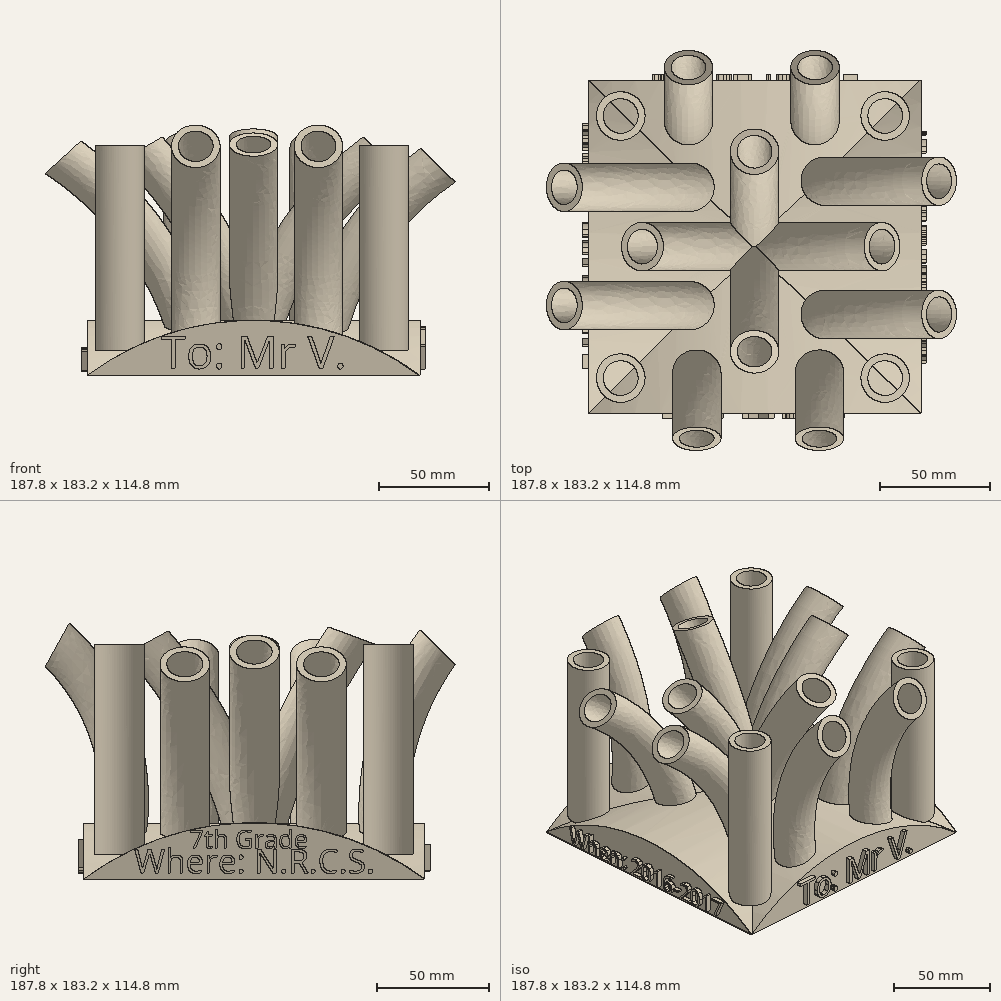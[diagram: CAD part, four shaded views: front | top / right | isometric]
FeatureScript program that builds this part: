
annotation { "Feature Type Name" : "Feature", "Feature Type Description" : "" }
export const myFeature = defineFeature(function(context is Context, id is Id, definition is map)
    precondition{}
    {
        {
            var Q0;
            Q0=qCreatedBy(makeId("Front.planeOp"),FACE);
            var sketch = newSketch(context, id + "F0", { "sketchPlane" : qUnion([Q0])});
            skLineSegment(sketch, "E0", {"start": v(0, -11.51) * mm, "end": v(-76.2, -11.51) * mm});
            skLineSegment(sketch, "E1", {"start": v(0, -11.51) * mm, "end": v(76.2, -11.51) * mm});
            skArc(sketch, "E2", {"start": v(76.2, -11.51) * mm, "mid": v(0, 13.89) * mm, "end": v(-76.2, -11.51) * mm});
            skSolve(sketch);
        }
        {
            var Q0;
            Q0 = qSketchRegion(id + "F0", true);
            extrude(context, id + "F1", {"entities" : qUnion([Q0]), "depth" : 76.2 * mm, "hasSecondDirection" : true, "secondDirectionOppositeDirection" : true, "secondDirectionDepth" : 76.2 * mm});
        }
        {
            var Q0;
            Q0=qCreatedBy(makeId("Right.planeOp"),FACE);
            var sketch = newSketch(context, id + "F2", { "sketchPlane" : qUnion([Q0])});
            skLineSegment(sketch, "E3", {"start": v(0, -11.22) * mm, "end": v(76.2, -11.22) * mm});
            skLineSegment(sketch, "E4", {"start": v(0, -11.22) * mm, "end": v(-76.2, -11.22) * mm});
            skArc(sketch, "E5", {"start": v(76.2, -11.22) * mm, "mid": v(0, 14.06) * mm, "end": v(-76.2, -11.22) * mm});
            skSolve(sketch);
        }
        {
            var Q0;
            Q0 = qSketchRegion(id + "F2", true);
            extrude(context, id + "F3", {"entities" : qUnion([Q0]), "operationType" : NewBodyOperationType.ADD, "depth" : 76.2 * mm, "hasSecondDirection" : true, "secondDirectionOppositeDirection" : true, "secondDirectionDepth" : 76.2 * mm});
        }
        {
            var Q0;
            Q0=qCreatedBy(makeId("Top.planeOp"),FACE);
            var sketch = newSketch(context, id + "F4", { "sketchPlane" : qUnion([Q0])});
            skCircle(sketch, "E6", {"center": v(0, 0) * mm, "radius": 11.11 * mm});
            skCircle(sketch, "E7", {"center": v(0, 0) * mm, "radius": 7.94 * mm});
            skSolve(sketch);
        }
        {
            var Q0;
            Q0=qCreatedBy(makeId("Front.planeOp"),FACE);
            var sketch = newSketch(context, id + "F5", { "sketchPlane" : qUnion([Q0])});
            skArc(sketch, "E8", {"start": v(0, 0) * mm, "mid": v(-19.55, 49.52) * mm, "end": v(-51.37, 92.2) * mm});
            skSolve(sketch);
        }
        {
            var Q0;
            Q0 = qSketchRegion(id + "F4", true);
            var Q1;
            Q1 = qConstructionFilter(qBodyType(qCreatedBy(id + "F5" ,EDGE), BodyType.WIRE), ConstructionObject.NO);
            sweep(context, id + "F6", {"operationType" : NewBodyOperationType.ADD, "profiles" : qUnion([Q0]), "path" : qUnion([Q1])});
        }
        {
            var Q0;
            Q0=qCreatedBy(makeId("Front.planeOp"),FACE);
            var sketch = newSketch(context, id + "F7", { "sketchPlane" : qUnion([Q0])});
            skArc(sketch, "E9", {"start": v(58.34, 90.31) * mm, "mid": v(20.67, 50.65) * mm, "end": v(0, 0) * mm});
            skSolve(sketch);
        }
        {
            var Q0;
            Q0 = qSketchRegion(id + "F4", true);
            var Q1;
            Q1 = qConstructionFilter(qBodyType(qCreatedBy(id + "F7" ,EDGE), BodyType.WIRE), ConstructionObject.NO);
            sweep(context, id + "F8", {"operationType" : NewBodyOperationType.ADD, "profiles" : qUnion([Q0]), "path" : qUnion([Q1])});
        }
        {
            var Q0;
            Q0=qCreatedBy(makeId("Right.planeOp"),FACE);
            var sketch = newSketch(context, id + "F9", { "sketchPlane" : qUnion([Q0])});
            skArc(sketch, "E10", {"start": v(1.27, 0) * mm, "mid": v(-16.91, 50.52) * mm, "end": v(-47, 94.99) * mm});
            skSolve(sketch);
        }
        {
            var Q0;
            Q0 = qSketchRegion(id + "F4", true);
            var Q1;
            Q1 = qConstructionFilter(qBodyType(qCreatedBy(id + "F9" ,EDGE), BodyType.WIRE), ConstructionObject.NO);
            sweep(context, id + "F10", {"operationType" : NewBodyOperationType.ADD, "profiles" : qUnion([Q0]), "path" : qUnion([Q1])});
        }
        {
            var Q0;
            Q0=qCreatedBy(makeId("Right.planeOp"),FACE);
            var sketch = newSketch(context, id + "F11", { "sketchPlane" : qUnion([Q0])});
            skArc(sketch, "E11", {"start": v(43.44, 97.68) * mm, "mid": v(17.36, 50.78) * mm, "end": v(0, 0) * mm});
            skSolve(sketch);
        }
        {
            var Q0;
            Q0 = qSketchRegion(id + "F4", true);
            var Q1;
            Q1 = qConstructionFilter(qBodyType(qCreatedBy(id + "F11" ,EDGE), BodyType.WIRE), ConstructionObject.NO);
            sweep(context, id + "F12", {"operationType" : NewBodyOperationType.ADD, "profiles" : qUnion([Q0]), "path" : qUnion([Q1])});
        }
        {
            var Q0;
            Q0=qCreatedBy(makeId("Top.planeOp"),FACE);
            var sketch = newSketch(context, id + "F13", { "sketchPlane" : qUnion([Q0])});
            skCircle(sketch, "E12", {"center": v(-26.33, 27.16) * mm, "radius": 11.11 * mm});
            skCircle(sketch, "E13", {"center": v(-26.33, 27.16) * mm, "radius": 7.94 * mm});
            skCircle(sketch, "E14", {"center": v(-26.33, -26.98) * mm, "radius": 11.11 * mm});
            skCircle(sketch, "E15", {"center": v(-26.33, -26.98) * mm, "radius": 7.94 * mm});
            skSolve(sketch);
        }
        {
            var Q0;
            Q0=qCreatedBy(makeId("Front.planeOp"),FACE);
            var sketch = newSketch(context, id + "F14", { "sketchPlane" : qUnion([Q0])});
            skArc(sketch, "E16", {"start": v(-26.38, 0) * mm, "mid": v(-48.5, 49.92) * mm, "end": v(-87.15, 88.47) * mm});
            skSolve(sketch);
        }
        {
            var Q0;
            Q0 = qSketchRegion(id + "F13", true);
            var Q1;
            Q1 = qConstructionFilter(qBodyType(qCreatedBy(id + "F14" ,EDGE), BodyType.WIRE), ConstructionObject.NO);
            sweep(context, id + "F15", {"operationType" : NewBodyOperationType.ADD, "profiles" : qUnion([Q0]), "path" : qUnion([Q1])});
        }
        {
            var Q0;
            Q0=qCreatedBy(makeId("Top.planeOp"),FACE);
            var sketch = newSketch(context, id + "F16", { "sketchPlane" : qUnion([Q0])});
            skCircle(sketch, "E17", {"center": v(29.75, 29.95) * mm, "radius": 11.11 * mm});
            skCircle(sketch, "E18", {"center": v(29.75, 29.95) * mm, "radius": 7.94 * mm});
            skCircle(sketch, "E19", {"center": v(29.75, -31.06) * mm, "radius": 11.11 * mm});
            skCircle(sketch, "E20", {"center": v(29.75, -31.06) * mm, "radius": 8.06 * mm});
            skSolve(sketch);
        }
        {
            var Q0;
            Q0=qCreatedBy(makeId("Front.planeOp"),FACE);
            var sketch = newSketch(context, id + "F17", { "sketchPlane" : qUnion([Q0])});
            skArc(sketch, "E21", {"start": v(84.52, 84.8) * mm, "mid": v(48.85, 47.76) * mm, "end": v(29.8, 0) * mm});
            skSolve(sketch);
        }
        {
            var Q0;
            Q0 = qSketchRegion(id + "F16", true);
            var Q1;
            Q1 = qConstructionFilter(qBodyType(qCreatedBy(id + "F17" ,EDGE), BodyType.WIRE), ConstructionObject.NO);
            sweep(context, id + "F18", {"operationType" : NewBodyOperationType.ADD, "profiles" : qUnion([Q0]), "path" : qUnion([Q1])});
        }
        {
            var Q0;
            Q0=qCreatedBy(makeId("Top.planeOp"),FACE);
            var sketch = newSketch(context, id + "F19", { "sketchPlane" : qUnion([Q0])});
            skCircle(sketch, "E22", {"center": v(-26.48, -61.1) * mm, "radius": 11.11 * mm});
            skCircle(sketch, "E23", {"center": v(-26.48, -61.1) * mm, "radius": 7.94 * mm});
            skCircle(sketch, "E24", {"center": v(29.7, -61.1) * mm, "radius": 11.11 * mm});
            skCircle(sketch, "E25", {"center": v(29.7, -61.1) * mm, "radius": 7.94 * mm});
            skSolve(sketch);
        }
        {
            var Q0;
            Q0=qCreatedBy(makeId("Right.planeOp"),FACE);
            var sketch = newSketch(context, id + "F20", { "sketchPlane" : qUnion([Q0])});
            skArc(sketch, "E26", {"start": v(-61.1, 0) * mm, "mid": v(-61.76, 50.45) * mm, "end": v(-87.94, 93.57) * mm});
            skSolve(sketch);
        }
        {
            var Q0;
            Q0 = qSketchRegion(id + "F19", true);
            var Q1;
            Q1 = qConstructionFilter(qBodyType(qCreatedBy(id + "F20" ,EDGE), BodyType.WIRE), ConstructionObject.NO);
            sweep(context, id + "F21", {"operationType" : NewBodyOperationType.ADD, "profiles" : qUnion([Q0]), "path" : qUnion([Q1])});
        }
        {
            var Q0;
            Q0=qCreatedBy(makeId("Top.planeOp"),FACE);
            var sketch = newSketch(context, id + "F22", { "sketchPlane" : qUnion([Q0])});
            skCircle(sketch, "E27", {"center": v(-30.26, 58.99) * mm, "radius": 11.11 * mm});
            skCircle(sketch, "E28", {"center": v(-30.26, 58.99) * mm, "radius": 7.94 * mm});
            skCircle(sketch, "E29", {"center": v(27.7, 58.99) * mm, "radius": 11.11 * mm});
            skCircle(sketch, "E30", {"center": v(27.7, 58.99) * mm, "radius": 7.94 * mm});
            skSolve(sketch);
        }
        {
            var Q0;
            Q0=qCreatedBy(makeId("Right.planeOp"),FACE);
            var sketch = newSketch(context, id + "F23", { "sketchPlane" : qUnion([Q0])});
            skArc(sketch, "E31", {"start": v(81.94, 92.52) * mm, "mid": v(61.17, 48.56) * mm, "end": v(58.9, 0) * mm});
            skSolve(sketch);
        }
        {
            var Q0;
            Q0 = qSketchRegion(id + "F22", true);
            var Q1;
            Q1 = qConstructionFilter(qBodyType(qCreatedBy(id + "F23" ,EDGE), BodyType.WIRE), ConstructionObject.NO);
            sweep(context, id + "F24", {"operationType" : NewBodyOperationType.ADD, "profiles" : qUnion([Q0]), "path" : qUnion([Q1])});
        }
        {
            var Q0;
            Q0=makeQuery(id+"F1.opExtrude","CAP_FACE",FACE,{"disambiguationData":[OSD([sQuery(id+"F0.wireOp",EDGE,"E0"),sQuery(id+"F0.wireOp",EDGE,"E1"),sQuery(id+"F0.wireOp",EDGE,"E2")])],"isStart":false});
            var sketch = newSketch(context, id + "F25", { "sketchPlane" : qUnion([Q0])});
            skText(sketch, "E32", { "text": "To: Mr V.", "fontName": "OpenSans-Regular.ttf"});
            const initialGuessF25  = {"E32": [-0.0423, -0.0082, 1, 0, 0.01484]};
            skSetInitialGuess(sketch, initialGuessF25);
            skSolve(sketch);
        }
        {
            var Q0;
            Q0 = qSketchRegion(id + "F25", true);
            extrude(context, id + "F26", {"entities" : qUnion([Q0]), "operationType" : NewBodyOperationType.ADD, "depth" : 2.54 * mm});
        }
        {
            var Q0;
            Q0=makeQuery(id+"F1.opExtrude","CAP_FACE",FACE,{"disambiguationData":[OSD([sQuery(id+"F0.wireOp",EDGE,"E0"),sQuery(id+"F0.wireOp",EDGE,"E1"),sQuery(id+"F0.wireOp",EDGE,"E2")])],"isStart":true});
            var sketch = newSketch(context, id + "F27", { "sketchPlane" : qUnion([Q0])});
            skText(sketch, "E33", { "text": "From: Karter", "fontName": "OpenSans-Regular.ttf"});
            const initialGuessF27  = {"E33": [-0.04861, -0.00747, 1, 0, 0.01169]};
            skSetInitialGuess(sketch, initialGuessF27);
            skSolve(sketch);
        }
        {
            var Q0;
            Q0 = qSketchRegion(id + "F27", true);
            extrude(context, id + "F28", {"entities" : qUnion([Q0]), "operationType" : NewBodyOperationType.ADD, "depth" : 2.54 * mm});
        }
        {
            var Q0;
            Q0=qCreatedBy(makeId("Top.planeOp"),FACE);
            var sketch = newSketch(context, id + "F29", { "sketchPlane" : qUnion([Q0])});
            skCircle(sketch, "E34", {"center": v(-61.28, 59.83) * mm, "radius": 11.11 * mm});
            skCircle(sketch, "E35", {"center": v(-61.28, 59.83) * mm, "radius": 7.94 * mm});
            skCircle(sketch, "E36", {"center": v(59.78, 59.83) * mm, "radius": 11.11 * mm});
            skCircle(sketch, "E37", {"center": v(59.78, 59.83) * mm, "radius": 7.94 * mm});
            skCircle(sketch, "E38", {"center": v(59.78, -60.2) * mm, "radius": 11.11 * mm});
            skCircle(sketch, "E39", {"center": v(59.78, -60.2) * mm, "radius": 7.94 * mm});
            skCircle(sketch, "E40", {"center": v(-61.28, -60.2) * mm, "radius": 11.11 * mm});
            skCircle(sketch, "E41", {"center": v(-61.28, -60.2) * mm, "radius": 7.94 * mm});
            skSolve(sketch);
        }
        {
            var Q0;
            Q0=qCreatedBy(makeId("Front.planeOp"),FACE);
            var sketch = newSketch(context, id + "F30", { "sketchPlane" : qUnion([Q0])});
            skLineSegment(sketch, "E42", {"start": v(-61.44, 0) * mm, "end": v(-61.44, 93.88) * mm});
            skSolve(sketch);
        }
        {
            var Q0;
            Q0 = qSketchRegion(id + "F29", true);
            var Q1;
            Q1 = qConstructionFilter(qBodyType(qCreatedBy(id + "F30" ,EDGE), BodyType.WIRE), ConstructionObject.NO);
            sweep(context, id + "F31", {"operationType" : NewBodyOperationType.ADD, "profiles" : qUnion([Q0]), "path" : qUnion([Q1])});
        }
        {
            var Q0;
            Q0=makeQuery(id+"F3.opExtrude","CAP_FACE",FACE,{"disambiguationData":[OSD([sQuery(id+"F2.wireOp",EDGE,"E3"),sQuery(id+"F2.wireOp",EDGE,"E4"),sQuery(id+"F2.wireOp",EDGE,"E5")])],"isStart":true});
            var sketch = newSketch(context, id + "F32", { "sketchPlane" : qUnion([Q0])});
            skText(sketch, "E43", { "text": "When: 2016-2017", "fontName": "OpenSans-Regular.ttf"});
            const initialGuessF32  = {"E43": [-0.05674, -0.00929, 1, 0, 0.01003]};
            skSetInitialGuess(sketch, initialGuessF32);
            skSolve(sketch);
        }
        {
            var Q0;
            Q0 = qSketchRegion(id + "F32", true);
            extrude(context, id + "F33", {"entities" : qUnion([Q0]), "operationType" : NewBodyOperationType.ADD, "depth" : 2.54 * mm});
        }
        {
            var Q0;
            Q0=makeQuery(id+"F3.opExtrude","CAP_FACE",FACE,{"disambiguationData":[OSD([sQuery(id+"F2.wireOp",EDGE,"E3"),sQuery(id+"F2.wireOp",EDGE,"E4"),sQuery(id+"F2.wireOp",EDGE,"E5")])],"isStart":false});
            var sketch = newSketch(context, id + "F34", { "sketchPlane" : qUnion([Q0])});
            skText(sketch, "E44", { "text": "Where: N.R.C.S.", "fontName": "OpenSans-Regular.ttf"});
            const initialGuessF34  = {"E44": [-0.05365, -0.0085, 1, 0, 0.01073]};
            skSetInitialGuess(sketch, initialGuessF34);
            skSolve(sketch);
        }
        {
            var Q0;
            Q0 = qSketchRegion(id + "F34", true);
            extrude(context, id + "F35", {"entities" : qUnion([Q0]), "operationType" : NewBodyOperationType.ADD, "depth" : 2.54 * mm});
        }
        {
            var Q0;
            {var subQ0=sQuery(id+"F2.wireOp",EDGE,"E4");var subQ1=sQuery(id+"F2.wireOp",EDGE,"E3");var subQ2=sQuery(id+"F2.wireOp",EDGE,"E5");Q0=makeQuery(id+"F35.boolean.opBoolean","SPLIT",FACE,{"disambiguationData":[TD([makeQuery(id+"F3.opExtrude","SWEPT_FACE",FACE,{"disambiguationData":[OSD([subQ2])]})])],"derivedFrom":makeQuery(id+"F3.opExtrude","CAP_FACE",FACE,{"disambiguationData":[OSD([subQ1,subQ0,subQ2])],"isStart":false})});}
            var sketch = newSketch(context, id + "F36", { "sketchPlane" : qUnion([Q0])});
            skText(sketch, "E45", { "text": "7th Grade\n", "fontName": "OpenSans-Regular.ttf"});
            const initialGuessF36  = {"E45": [-0.02894, 0.00257, 1, 0, 0.00817]};
            skSetInitialGuess(sketch, initialGuessF36);
            skSolve(sketch);
        }
        {
            var Q0;
            Q0 = qSketchRegion(id + "F36", true);
            extrude(context, id + "F37", {"entities" : qUnion([Q0]), "operationType" : NewBodyOperationType.ADD, "depth" : 2.54 * mm});
        }
    });
